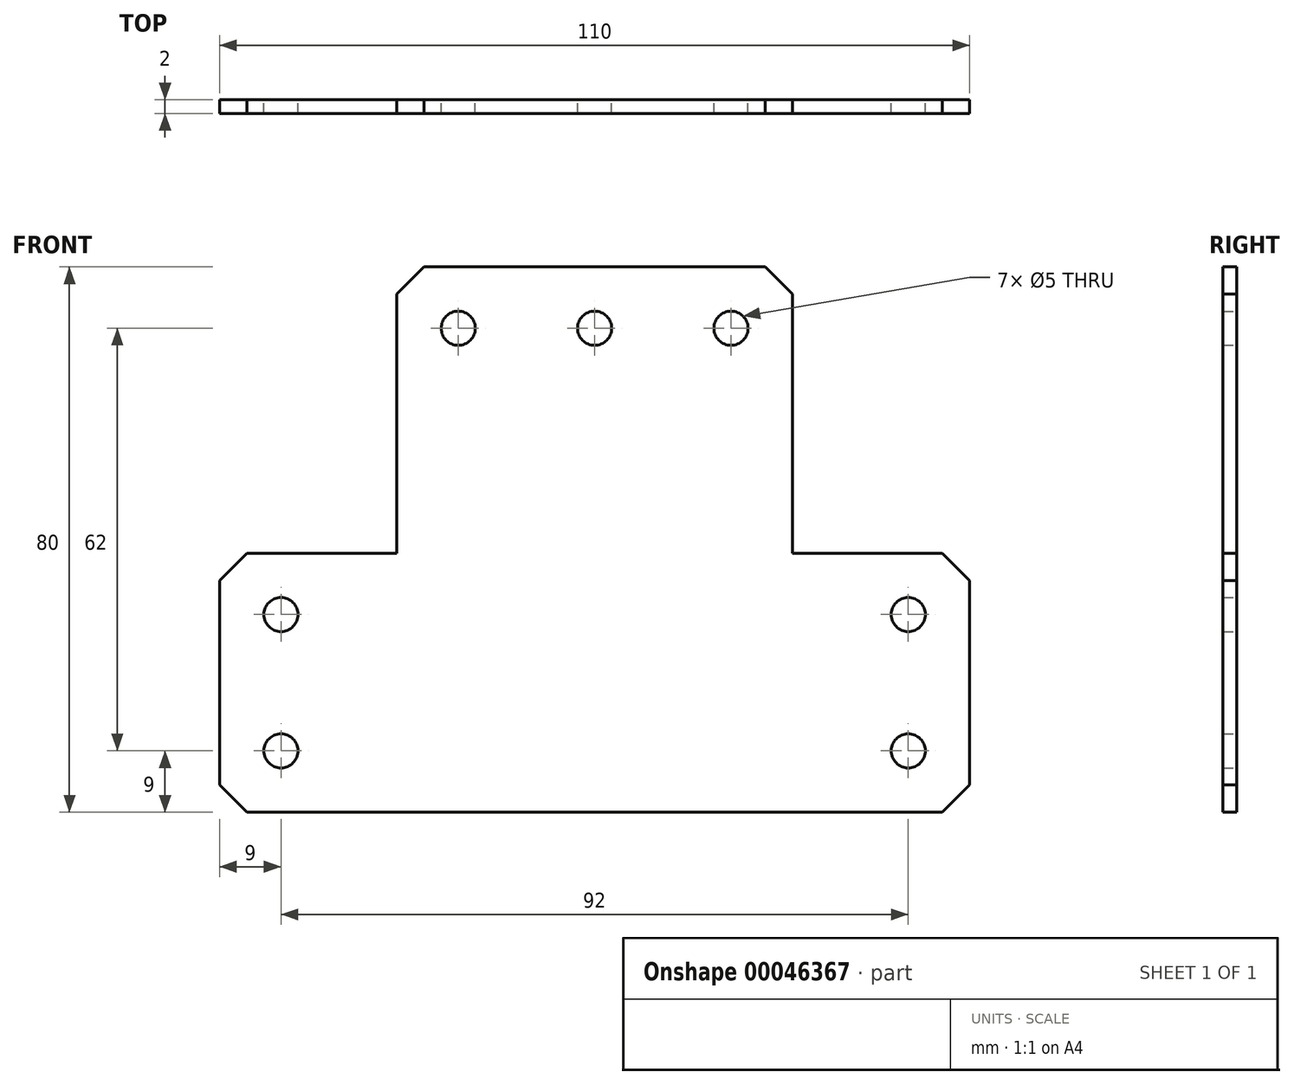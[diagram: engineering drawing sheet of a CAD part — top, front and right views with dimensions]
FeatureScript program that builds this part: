
annotation { "Feature Type Name" : "Feature", "Feature Type Description" : "" }
export const myFeature = defineFeature(function(context is Context, id is Id, definition is map)
    precondition{}
    {
        {
            var Q0;
            Q0=qCreatedBy(makeId("Front.planeOp"),FACE);
            var sketch = newSketch(context, id + "F0", { "sketchPlane" : qUnion([Q0])});
            skLineSegment(sketch, "E0", {"start": v(-110, 0) * mm, "end": v(0, 0) * mm});
            skLineSegment(sketch, "E1", {"start": v(0, 0) * mm, "end": v(0, 38) * mm});
            skLineSegment(sketch, "E2", {"start": v(0, 38) * mm, "end": v(-26, 38) * mm});
            skLineSegment(sketch, "E3", {"start": v(-26, 38) * mm, "end": v(-26, 80) * mm});
            skLineSegment(sketch, "E4", {"start": v(-26, 80) * mm, "end": v(-84, 80) * mm});
            skLineSegment(sketch, "E5", {"start": v(-84, 80) * mm, "end": v(-84, 38) * mm});
            skLineSegment(sketch, "E6", {"start": v(-84, 38) * mm, "end": v(-110, 38) * mm});
            skLineSegment(sketch, "E7", {"start": v(-110, 38) * mm, "end": v(-110, 0) * mm});
            skCircle(sketch, "E8", {"center": v(-101, 29) * mm, "radius": 2.5 * mm});
            skLineSegment(sketch, "E9", {"start": v(-55, 80) * mm, "end": v(-55, 0) * mm, "construction": true});
            skLineSegment(sketch, "E10", {"start": v(-110, 19) * mm, "end": v(0, 19) * mm, "construction": true});
            skCircle(sketch, "E11", {"center": v(-75, 71) * mm, "radius": 2.5 * mm});
            skCircle(sketch, "E12.0.MirrorC", {"center": v(-35, 71) * mm, "radius": 2.5 * mm});
            skCircle(sketch, "E13.0.MirrorC", {"center": v(-9, 29) * mm, "radius": 2.5 * mm});
            skCircle(sketch, "E14.0.MirrorC", {"center": v(-101, 9) * mm, "radius": 2.5 * mm});
            skCircle(sketch, "E15.0.MirrorC", {"center": v(-9, 9) * mm, "radius": 2.5 * mm});
            skCircle(sketch, "E16", {"center": v(-55, 71) * mm, "radius": 2.5 * mm});
            skSolve(sketch);
        }
        {
            var Q0;
            Q0=makeQuery(id+"F0.imprint","IMPRINT",FACE,{"disambiguationData":[TD([[makeQuery(id+"F0.imprint","IMPRINT",EDGE,{"derivedFrom":sQuery(id+"F0.wireOp",EDGE,"E0")}),1.0]])]});
            extrude(context, id + "F1", {"entities" : qUnion([Q0]), "depth" : 2 * mm});
        }
        {
            var Q0;
            Q0=makeQuery(id+"F1.opExtrude","SWEPT_EDGE",EDGE,{"disambiguationData":[OSD([sQuery(id+"F0.wireOp",EDGE,"E3"),sQuery(id+"F0.wireOp",EDGE,"E4")])]});
            var Q1;
            Q1=makeQuery(id+"F1.opExtrude","SWEPT_EDGE",EDGE,{"disambiguationData":[OSD([sQuery(id+"F0.wireOp",EDGE,"E4"),sQuery(id+"F0.wireOp",EDGE,"E5")])]});
            var Q2;
            Q2=makeQuery(id+"F1.opExtrude","SWEPT_EDGE",EDGE,{"disambiguationData":[OSD([sQuery(id+"F0.wireOp",EDGE,"E1"),sQuery(id+"F0.wireOp",EDGE,"E2")])]});
            var Q3;
            Q3=makeQuery(id+"F1.opExtrude","SWEPT_EDGE",EDGE,{"disambiguationData":[OSD([sQuery(id+"F0.wireOp",EDGE,"E6"),sQuery(id+"F0.wireOp",EDGE,"E7")])]});
            var Q4;
            Q4=makeQuery(id+"F1.opExtrude","SWEPT_EDGE",EDGE,{"disambiguationData":[OSD([sQuery(id+"F0.wireOp",EDGE,"E0"),sQuery(id+"F0.wireOp",EDGE,"E1")])]});
            var Q5;
            Q5=makeQuery(id+"F1.opExtrude","SWEPT_EDGE",EDGE,{"disambiguationData":[OSD([sQuery(id+"F0.wireOp",EDGE,"E0"),sQuery(id+"F0.wireOp",EDGE,"E7")])]});
            chamfer(context, id + "F2", {"entities" : qUnion([Q0, Q1, Q2, Q3, Q4, Q5]), "width" : 4 * mm, "tangentPropagation" : true});
        }
    });
